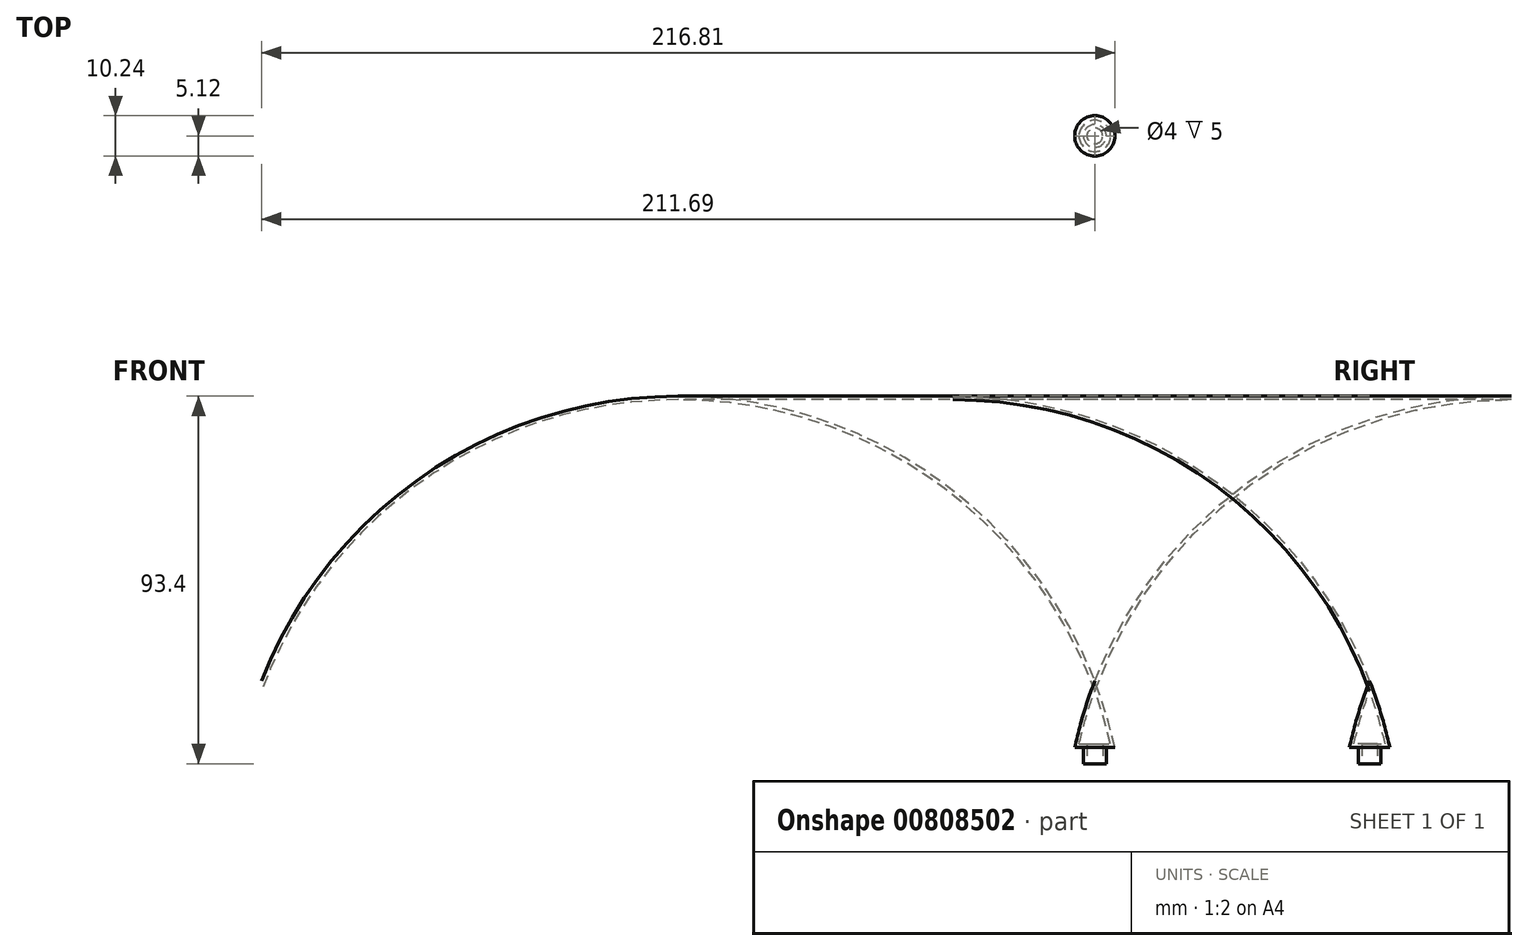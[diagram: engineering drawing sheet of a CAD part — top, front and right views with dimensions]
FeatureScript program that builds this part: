
annotation { "Feature Type Name" : "Feature", "Feature Type Description" : "" }
export const myFeature = defineFeature(function(context is Context, id is Id, definition is map)
    precondition{}
    {
        {
            var Q0;
            Q0=qCreatedBy(makeId("Front.planeOp"),FACE);
            var sketch = newSketch(context, id + "F0", { "sketchPlane" : qUnion([Q0])});
            skLineSegment(sketch, "E0", {"start": v(0, 0) * mm, "end": v(0, 18.5) * mm});
            skLineSegment(sketch, "E1", {"start": v(0, 0) * mm, "end": v(2, 0) * mm});
            skLineSegment(sketch, "E2", {"start": v(2, 0) * mm, "end": v(2, 5) * mm});
            skLineSegment(sketch, "E3", {"start": v(2, 5) * mm, "end": v(4, 5) * mm});
            skArc(sketch, "E4", {"start": v(4, 5) * mm, "mid": v(2.21, 11.81) * mm, "end": v(0, 18.5) * mm});
            skArc(sketch, "E5.0", {"start": v(5.12, 4.1) * mm, "mid": v(2.9, 12.67) * mm, "end": v(0, 21.05) * mm});
            skLineSegment(sketch, "E5.1", {"start": v(2.9, 4.1) * mm, "end": v(5.12, 4.1) * mm});
            skLineSegment(sketch, "E5.2", {"start": v(2.9, 0) * mm, "end": v(2.9, 4.1) * mm});
            skLineSegment(sketch, "E6", {"start": v(2, 0) * mm, "end": v(2.9, 0) * mm});
            skLineSegment(sketch, "E7", {"start": v(0, 18.5) * mm, "end": v(0, 21.05) * mm});
            skSolve(sketch);
        }
        {
            var Q0;
            Q0=makeQuery(id+"F0.imprint","IMPRINT",FACE,{"disambiguationData":[TD([[makeQuery(id+"F0.imprint","IMPRINT",EDGE,{"derivedFrom":sQuery(id+"F0.wireOp",EDGE,"E2")}),-1.0]])]});
            var Q1;
            Q1=sQuery(id+"F0.wireOp",EDGE,"E0");
            revolve(context, id + "F1", {"surfaceOperationType" : NewSurfaceOperationType.NEW, "entities" : qUnion([Q0]), "axis" : qUnion([Q1]), "revolveType" : RevolveType.FULL});
        }
    });
